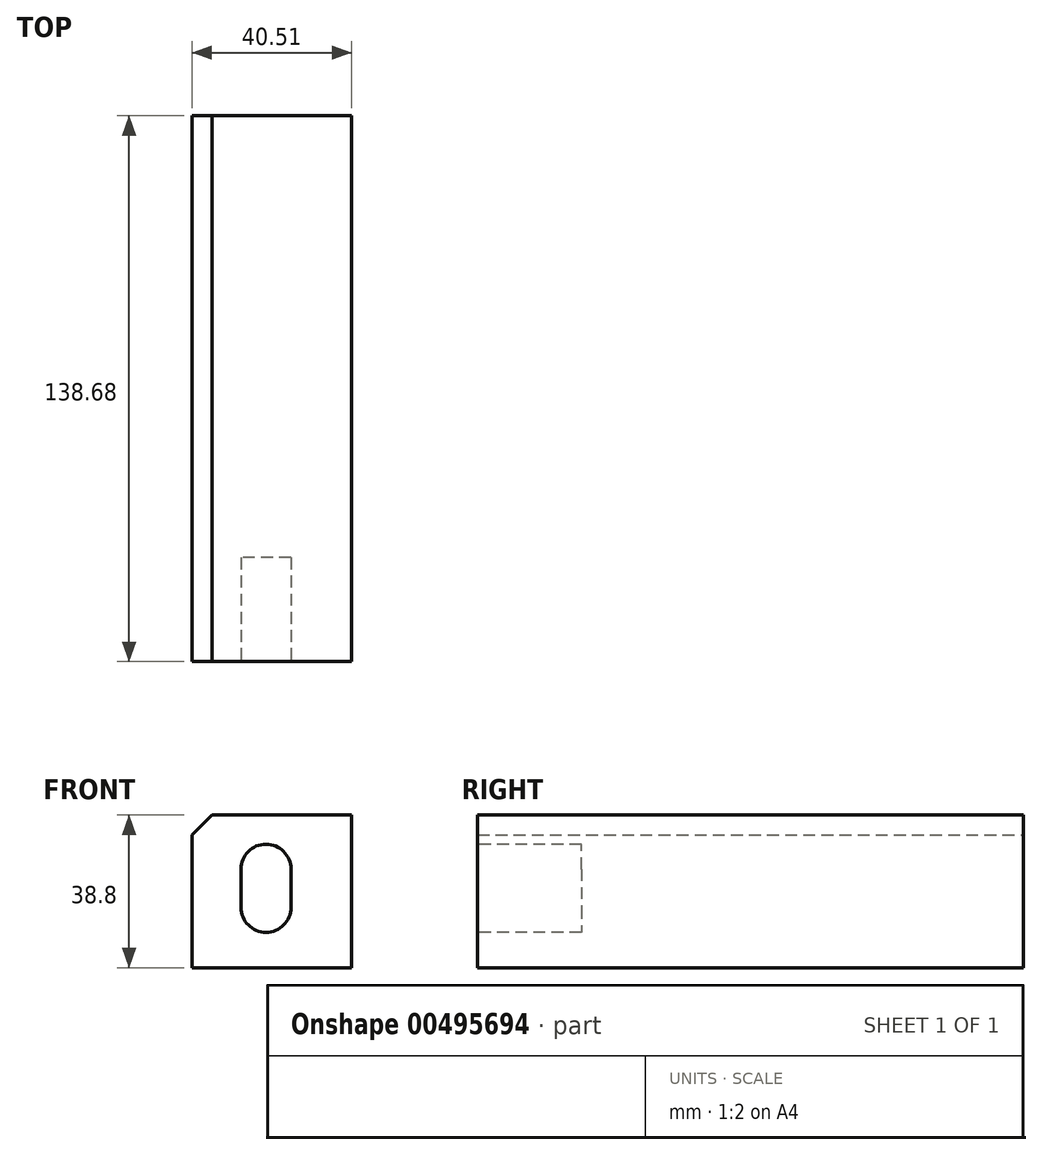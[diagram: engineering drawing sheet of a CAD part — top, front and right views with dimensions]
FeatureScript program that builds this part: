
annotation { "Feature Type Name" : "Feature", "Feature Type Description" : "" }
export const myFeature = defineFeature(function(context is Context, id is Id, definition is map)
    precondition{}
    {
        {
            var Q0;
            Q0=qCreatedBy(makeId("Front.planeOp"),FACE);
            var sketch = newSketch(context, id + "F0", { "sketchPlane" : qUnion([Q0])});
            skLineSegment(sketch, "E0", {"start": v(0, 0) * mm, "end": v(0, 38.8) * mm});
            skLineSegment(sketch, "E1", {"start": v(0, 38.8) * mm, "end": v(40.5, 38.8) * mm});
            skLineSegment(sketch, "E2", {"start": v(40.5, 38.8) * mm, "end": v(40.5, 0) * mm});
            skLineSegment(sketch, "E3", {"start": v(40.5, 0) * mm, "end": v(0, 0) * mm});
            skSolve(sketch);
        }
        {
            var Q0;
            Q0=makeQuery(id+"F0.imprint","IMPRINT",FACE,{"disambiguationData":[TD([[makeQuery(id+"F0.imprint","IMPRINT",EDGE,{"derivedFrom":sQuery(id+"F0.wireOp",EDGE,"E0")}),-1.0]])]});
            extrude(context, id + "F1", {"entities" : qUnion([Q0]), "depth" : 138.68 * mm});
        }
        {
            var Q0;
            Q0=makeQuery(id+"F1.opExtrude","SWEPT_EDGE",EDGE,{"disambiguationData":[OSD([sQuery(id+"F0.wireOp",EDGE,"E0"),sQuery(id+"F0.wireOp",EDGE,"E1")])]});
            chamfer(context, id + "F2", {"entities" : qUnion([Q0]), "width" : 5.08 * mm, "tangentPropagation" : true});
        }
        {
            var Q0;
            Q0=makeQuery(id+"F1.opExtrude","CAP_FACE",FACE,{"disambiguationData":[OSD([sQuery(id+"F0.wireOp",EDGE,"E0"),sQuery(id+"F0.wireOp",EDGE,"E1"),sQuery(id+"F0.wireOp",EDGE,"E2"),sQuery(id+"F0.wireOp",EDGE,"E3")])],"isStart":false});
            var sketch = newSketch(context, id + "F3", { "sketchPlane" : qUnion([Q0])});
            skSolve(sketch);
        }
        {
            var Q0;
            {var subQ2=sQuery(id+"F0.wireOp",EDGE,"E2");Q0=makeQuery(id+"F3.imprint","IMPRINT",FACE,{"disambiguationData":[TD([[makeQuery(id+"F3.imprint","IMPRINT",EDGE,{"derivedFrom":makeQuery(id+"F1.opExtrude","CAP_EDGE",EDGE,{"disambiguationData":[OSD([subQ2])],"isStart":false})}),-1.0]])]});}
            var sketch = newSketch(context, id + "F4", { "sketchPlane" : qUnion([Q0])});
            skLineSegment(sketch, "E4", {"start": v(18.78, 25.05) * mm, "end": v(18.78, 15.37) * mm});
            skArc(sketch, "E5.0.startCap", {"start": v(12.43, 25.05) * mm, "mid": v(18.78, 31.4) * mm, "end": v(25.13, 25.05) * mm});
            skArc(sketch, "E5.0.endCap", {"start": v(25.13, 15.37) * mm, "mid": v(18.78, 9.02) * mm, "end": v(12.43, 15.37) * mm});
            skLineSegment(sketch, "E5.0.left", {"start": v(25.13, 25.05) * mm, "end": v(25.13, 15.37) * mm});
            skLineSegment(sketch, "E5.0.right", {"start": v(12.43, 25.05) * mm, "end": v(12.43, 15.37) * mm});
            skSolve(sketch);
        }
        {
            var Q0;
            Q0=makeQuery(id+"F4.imprint","IMPRINT",FACE,{"disambiguationData":[TD([[makeQuery(id+"F4.imprint","IMPRINT",EDGE,{"derivedFrom":sQuery(id+"F4.wireOp",EDGE,"E5.0.startCap")}),1.0]])]});
            extrude(context, id + "F5", {"entities" : qUnion([Q0]), "operationType" : NewBodyOperationType.REMOVE, "oppositeDirection" : true, "depth" : 26.42 * mm});
        }
    });
